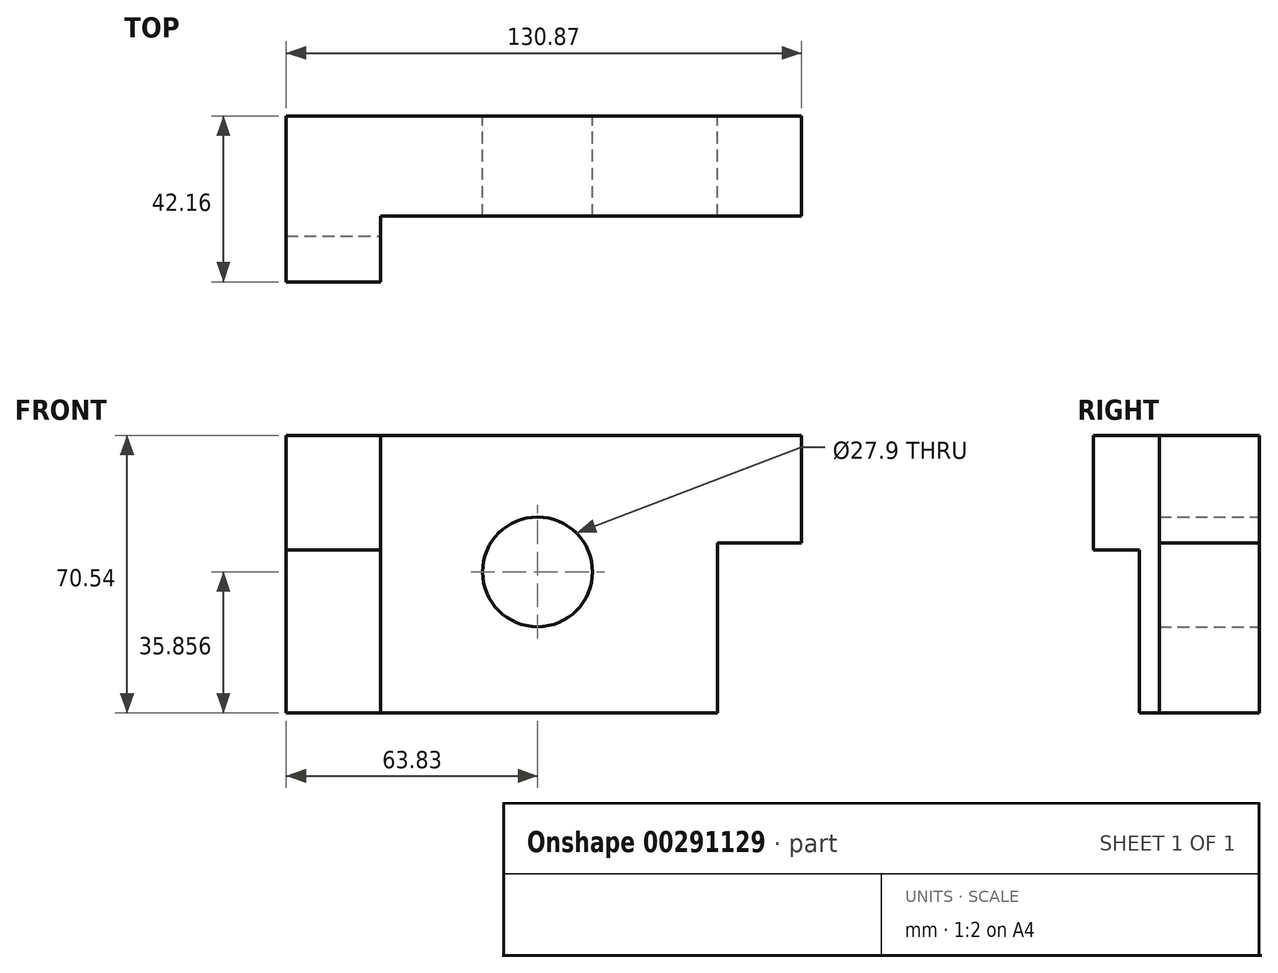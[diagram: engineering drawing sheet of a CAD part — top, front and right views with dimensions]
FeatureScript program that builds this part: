
annotation { "Feature Type Name" : "Feature", "Feature Type Description" : "" }
export const myFeature = defineFeature(function(context is Context, id is Id, definition is map)
    precondition{}
    {
        {
            var Q0;
            Q0=qCreatedBy(makeId("Front.planeOp"),FACE);
            var sketch = newSketch(context, id + "F0", { "sketchPlane" : qUnion([Q0])});
            skLineSegment(sketch, "E0.bottom", {"start": v(-63.83, 38.91) * mm, "end": v(67.04, 38.91) * mm});
            skLineSegment(sketch, "E0.top", {"start": v(-63.83, -31.63) * mm, "end": v(67.04, -31.63) * mm});
            skLineSegment(sketch, "E0.left", {"start": v(-63.83, 38.91) * mm, "end": v(-63.83, -31.63) * mm});
            skLineSegment(sketch, "E0.right", {"start": v(67.04, 38.91) * mm, "end": v(67.04, -31.63) * mm});
            skCircle(sketch, "E1", {"center": v(0, 4.23) * mm, "radius": 13.95 * mm});
            skSolve(sketch);
        }
        {
            var Q0;
            Q0 = qSketchRegion(id + "F0", true);
            extrude(context, id + "F1", {"entities" : qUnion([Q0]), "depth" : 25.4 * mm});
        }
        {
            var Q0;
            Q0=qCreatedBy(makeId("Front.planeOp"),FACE);
            var sketch = newSketch(context, id + "F2", { "sketchPlane" : qUnion([Q0])});
            skLineSegment(sketch, "E2.bottom", {"start": v(67.33, 11.51) * mm, "end": v(45.76, 11.51) * mm});
            skLineSegment(sketch, "E2.top", {"start": v(67.33, -31.63) * mm, "end": v(45.76, -31.63) * mm});
            skLineSegment(sketch, "E2.left", {"start": v(67.33, 11.51) * mm, "end": v(67.33, -31.63) * mm});
            skLineSegment(sketch, "E2.right", {"start": v(45.76, 11.51) * mm, "end": v(45.76, -31.63) * mm});
            skSolve(sketch);
        }
        {
            var Q0;
            Q0 = qSketchRegion(id + "F2", true);
            extrude(context, id + "F3", {"entities" : qUnion([Q0]), "operationType" : NewBodyOperationType.REMOVE, "depth" : 40.4 * mm});
        }
        {
            var Q0;
            Q0=qCreatedBy(makeId("Front.planeOp"),FACE);
            var sketch = newSketch(context, id + "F4", { "sketchPlane" : qUnion([Q0])});
            skLineSegment(sketch, "E3.bottom", {"start": v(-63.83, 9.76) * mm, "end": v(-39.93, 9.76) * mm});
            skLineSegment(sketch, "E3.top", {"start": v(-63.83, -31.63) * mm, "end": v(-39.93, -31.63) * mm});
            skLineSegment(sketch, "E3.left", {"start": v(-63.83, 9.76) * mm, "end": v(-63.83, -31.63) * mm});
            skLineSegment(sketch, "E3.right", {"start": v(-39.93, 9.76) * mm, "end": v(-39.93, -31.63) * mm});
            skSolve(sketch);
        }
        {
            var Q0;
            Q0 = qSketchRegion(id + "F4", true);
            extrude(context, id + "F5", {"entities" : qUnion([Q0]), "operationType" : NewBodyOperationType.ADD, "depth" : 30.48 * mm});
        }
        {
            var Q0;
            Q0=qCreatedBy(makeId("Front.planeOp"),FACE);
            var sketch = newSketch(context, id + "F6", { "sketchPlane" : qUnion([Q0])});
            skLineSegment(sketch, "E4.bottom", {"start": v(-63.83, 38.91) * mm, "end": v(-39.93, 38.91) * mm});
            skLineSegment(sketch, "E4.top", {"start": v(-63.83, 9.76) * mm, "end": v(-39.93, 9.76) * mm});
            skLineSegment(sketch, "E4.left", {"start": v(-63.83, 38.91) * mm, "end": v(-63.83, 9.76) * mm});
            skLineSegment(sketch, "E4.right", {"start": v(-39.93, 38.91) * mm, "end": v(-39.93, 9.76) * mm});
            skSolve(sketch);
        }
        {
            var Q0;
            Q0 = qSketchRegion(id + "F6", true);
            extrude(context, id + "F7", {"entities" : qUnion([Q0]), "operationType" : NewBodyOperationType.ADD, "depth" : 42.16 * mm});
        }
    });
